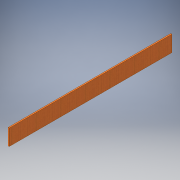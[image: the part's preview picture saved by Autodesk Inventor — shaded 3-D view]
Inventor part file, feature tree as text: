
AUTODESK INVENTOR PART (.ipt)
format: ipt  version: 2016 (Build 200138000, 138)  size: 94,720 bytes
history: native  units: in
note: dims shown in document units (in); Inventor stores cm internally (conversion verified against a paired STEP export)
features: extrude x1, sketch x1
ambient origin geometry x8: Origin, YZ Plane, XZ Plane, XY Plane, X Axis, Y Axis, Z Axis, Center Point
bodies: Solid1 (feature_tree)
feature tree (2):
  extrude  "Extrusion1"  Depth=6.5in
  sketch  "Sketch1"  dims[d0=66.1875in d1=6.5in d2=0.4375in d3=0.0in]
